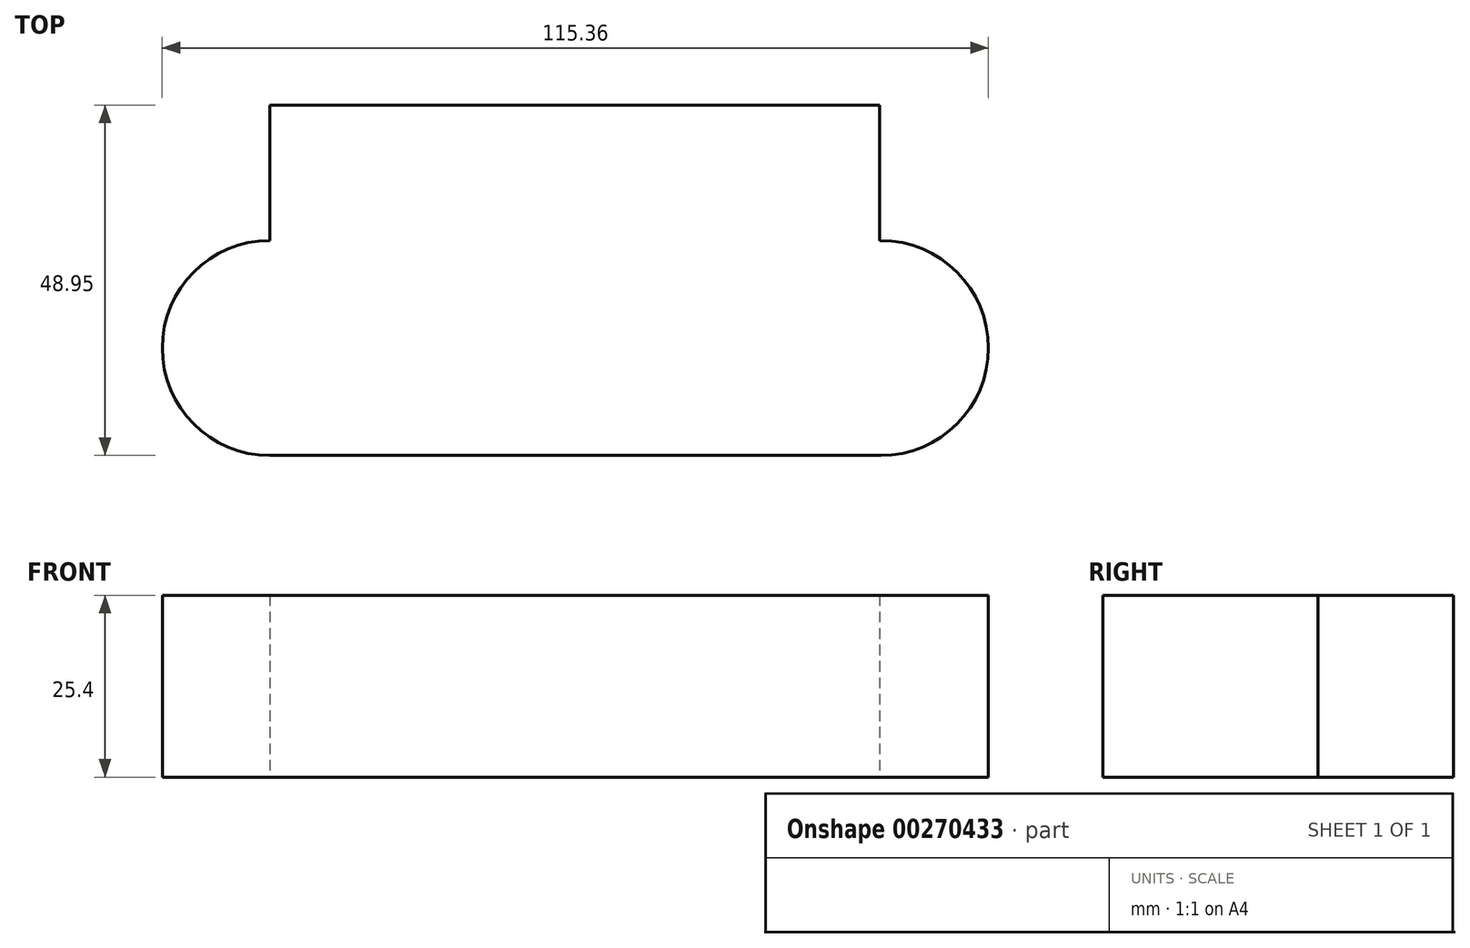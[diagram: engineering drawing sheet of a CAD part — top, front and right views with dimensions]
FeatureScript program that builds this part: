
annotation { "Feature Type Name" : "Feature", "Feature Type Description" : "" }
export const myFeature = defineFeature(function(context is Context, id is Id, definition is map)
    precondition{}
    {
        {
            var Q0;
            Q0=qCreatedBy(makeId("Top.planeOp"),FACE);
            var sketch = newSketch(context, id + "F0", { "sketchPlane" : qUnion([Q0])});
            skLineSegment(sketch, "E0", {"start": v(-44.24, -30.02) * mm, "end": v(40.48, -30.02) * mm});
            skArc(sketch, "E1", {"start": v(-44.24, -30.02) * mm, "mid": v(-59.25, -15) * mm, "end": v(-44.24, 0) * mm});
            skLineSegment(sketch, "E2", {"start": v(-44.24, 0) * mm, "end": v(41.1, 0) * mm});
            skArc(sketch, "E3", {"start": v(41.1, 0) * mm, "mid": v(56.11, -15) * mm, "end": v(41.1, -30.02) * mm});
            skPoint(sketch, "E4.startSnap0", {"position": v(-1.57, 0) * mm});
            skLineSegment(sketch, "E5", {"start": v(-1.57, 0) * mm, "end": v(41.1, 0) * mm});
            skLineSegment(sketch, "E6", {"start": v(0, 0) * mm, "end": v(41.1, 0) * mm});
            skLineSegment(sketch, "E7", {"start": v(-1.57, -30.02) * mm, "end": v(41.1, -30.02) * mm});
            skLineSegment(sketch, "E8.bottom", {"start": v(-44.24, 0) * mm, "end": v(40.9, 0) * mm});
            skLineSegment(sketch, "E8.top", {"start": v(-44.24, 18.93) * mm, "end": v(40.9, 18.93) * mm});
            skLineSegment(sketch, "E8.left", {"start": v(-44.24, 0) * mm, "end": v(-44.24, 18.93) * mm});
            skLineSegment(sketch, "E8.right", {"start": v(40.9, 0) * mm, "end": v(40.9, 18.93) * mm});
            skPoint(sketch, "E9", {"position": v(0, 10.35) * mm});
            skPoint(sketch, "E10", {"position": v(29.35, 10.35) * mm});
            skPoint(sketch, "E11.MirrorP", {"position": v(-117.83, 10.35) * mm});
            skPoint(sketch, "E12", {"position": v(-33.15, 10.35) * mm});
            skSolve(sketch);
        }
        {
            var Q0;
            Q0 = qSketchRegion(id + "F0", true);
            extrude(context, id + "F1", {"entities" : qUnion([Q0]), "depth" : 25.4 * mm});
        }
    });
